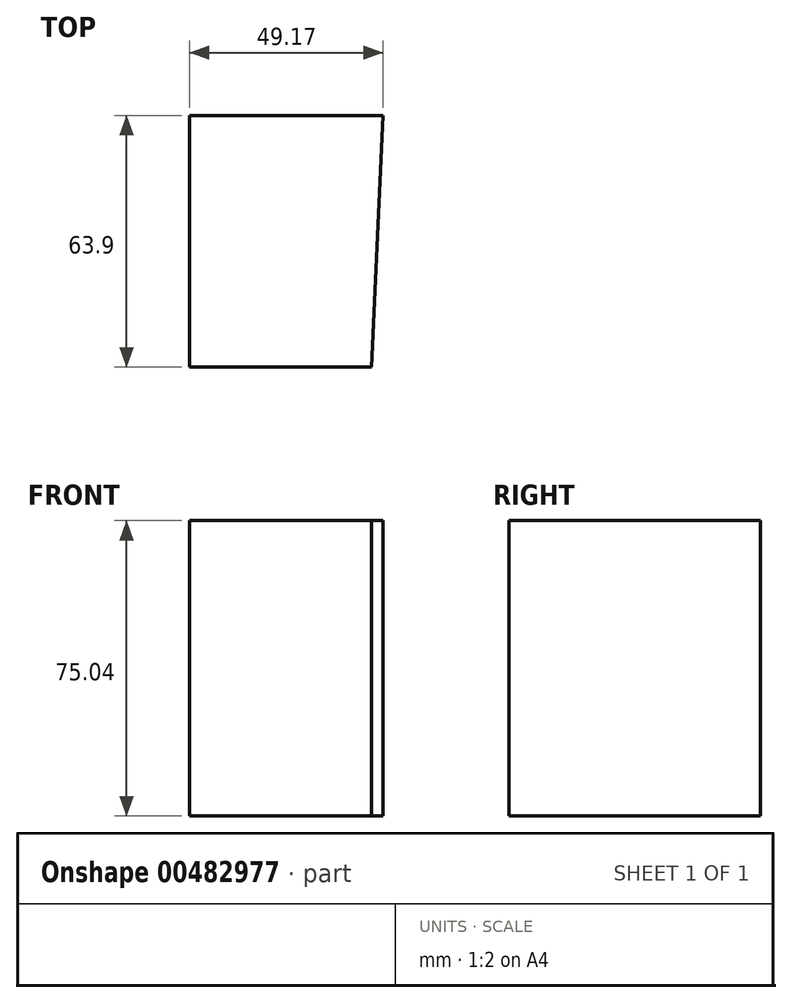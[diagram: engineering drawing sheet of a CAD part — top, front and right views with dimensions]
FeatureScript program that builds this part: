
annotation { "Feature Type Name" : "Feature", "Feature Type Description" : "" }
export const myFeature = defineFeature(function(context is Context, id is Id, definition is map)
    precondition{}
    {
        {
            var Q0;
            Q0=qCreatedBy(makeId("Top.planeOp"),FACE);
            var sketch = newSketch(context, id + "F0", { "sketchPlane" : qUnion([Q0])});
            skLineSegment(sketch, "E0", {"start": v(-23.86, -27.8) * mm, "end": v(22.4, -27.8) * mm});
            skLineSegment(sketch, "E1", {"start": v(-23.86, 36.1) * mm, "end": v(-23.86, -27.8) * mm});
            skLineSegment(sketch, "E2", {"start": v(25.3, 36.1) * mm, "end": v(-23.86, 36.1) * mm});
            skLineSegment(sketch, "E3", {"start": v(22.4, -27.8) * mm, "end": v(25.3, 36.1) * mm});
            skSolve(sketch);
        }
        {
            var Q0;
            Q0=makeQuery(id+"F0.imprint","IMPRINT",FACE,{"disambiguationData":[TD([[makeQuery(id+"F0.imprint","IMPRINT",EDGE,{"derivedFrom":sQuery(id+"F0.wireOp",EDGE,"E0")}),1.0]])]});
            extrude(context, id + "F1", {"entities" : qUnion([Q0]), "depth" : 25.4 * mm, "hasSecondDirection" : true, "secondDirectionOppositeDirection" : true, "secondDirectionDepth" : 49.64 * mm});
        }
    });
